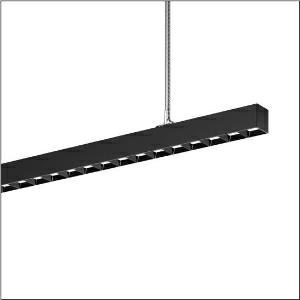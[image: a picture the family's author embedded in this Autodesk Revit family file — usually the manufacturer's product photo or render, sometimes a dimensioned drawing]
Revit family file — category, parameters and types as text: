
# Revit family: silica_r__21_51mx32tctdb_2a66
name_source: partatom
category: Lighting Fixtures
units: mm (PartAtom-declared; Revit-internal decimal feet)

## family parameters
Cut with Voids When Loaded = No
Host = Face
Light Source = No
Part Type = Normal
Room Calculation Point = No
Round Connector Dimension = Use Diameter
Shared = No

## types (1)
- --- (1 x LED, 15540 lm, 133.6 W, 6500K)
    Apparent Load = 134 VA
    CIE Flux Codes = 84 99 100 60 100
    Color Rendering = 80
    Color Temperature = 6500K
    Default Elevation = 1800 mm
    Description = Silica® 21, office luminaire, primary light control with darklight reflector, of PMMA, black, CAT 2 (L<= 3000cd/m²), light emission: direct/indirect distribution, primary light characteristic: symmetric, installation type: suspended mounting, LED, rated luminous flux: 15.540lm, luminous efficacy: 111lm/W, light colour: 8tw, colour temperature: 2700..6500K, control gear: ECG DALI, with terminal, 3+2-pole, max. 2.5mm², mains connection: 220..240V, AC, 50/60Hz, rated input power: 140.3W, luminaire housing, of aluminium, jet black (RAL 9005), length: 3.004mm, width: 53mm, height: 53mm, protection rating (complete): IP20, insulation class (complete): insulation class I (protective earthing), certification: CE, permissible operating ambient temperature: 0..+35°C, standard: EN 50419, packaging unit: 1 piece
    Height = 53 mm
    Lamp = 1 x LED
    Lamp Light Flux = 15540 lm
    Lamp Power = 133.6 W
    Lamp count = 1
    Length = 3004 mm
    Luminous efficacy = 116 lm/W
    Manufacturer = Siteco
    ModVariant = No
    Model = 51MX32TCTDB
    Mounting Place = Ceiling
    Mounting Type = Pendant
    Number of Poles = 1
    OnlyDefault = Yes
    Power Factor = 1
    Product Name = Silica® 21
    Product group = office luminaire | ceiling pendant
    ProductGroupID = 902
    Protection Class = Protection class I
    Protection Degree = IP 20
    RLX_Detail_Level = 1
    RLX_Emergency_Light_Flux = 0 lm
    RLX_Emergency_Type = 0
    RLX_Emergency_Type_DB = No
    RlxData = <blob elided: 63913 chars, md5=bf847fb9>
    Socket = socket
    Standby Power = 0 W
    System Light Flux = 15540 lm
    System Power = 134 W
    Type Comments = individual setting
    Type Image = l_1297774.jpg
    URL = http://relux.com
    VarID = @adj_071257
    Voltage = 0 V
    Weight = 0.00 kg
    Width = 53 mm

## geometry (parser evidence)
native form markers: Blend x4, Sweep x11
no freeform markers — native parametric forms only
